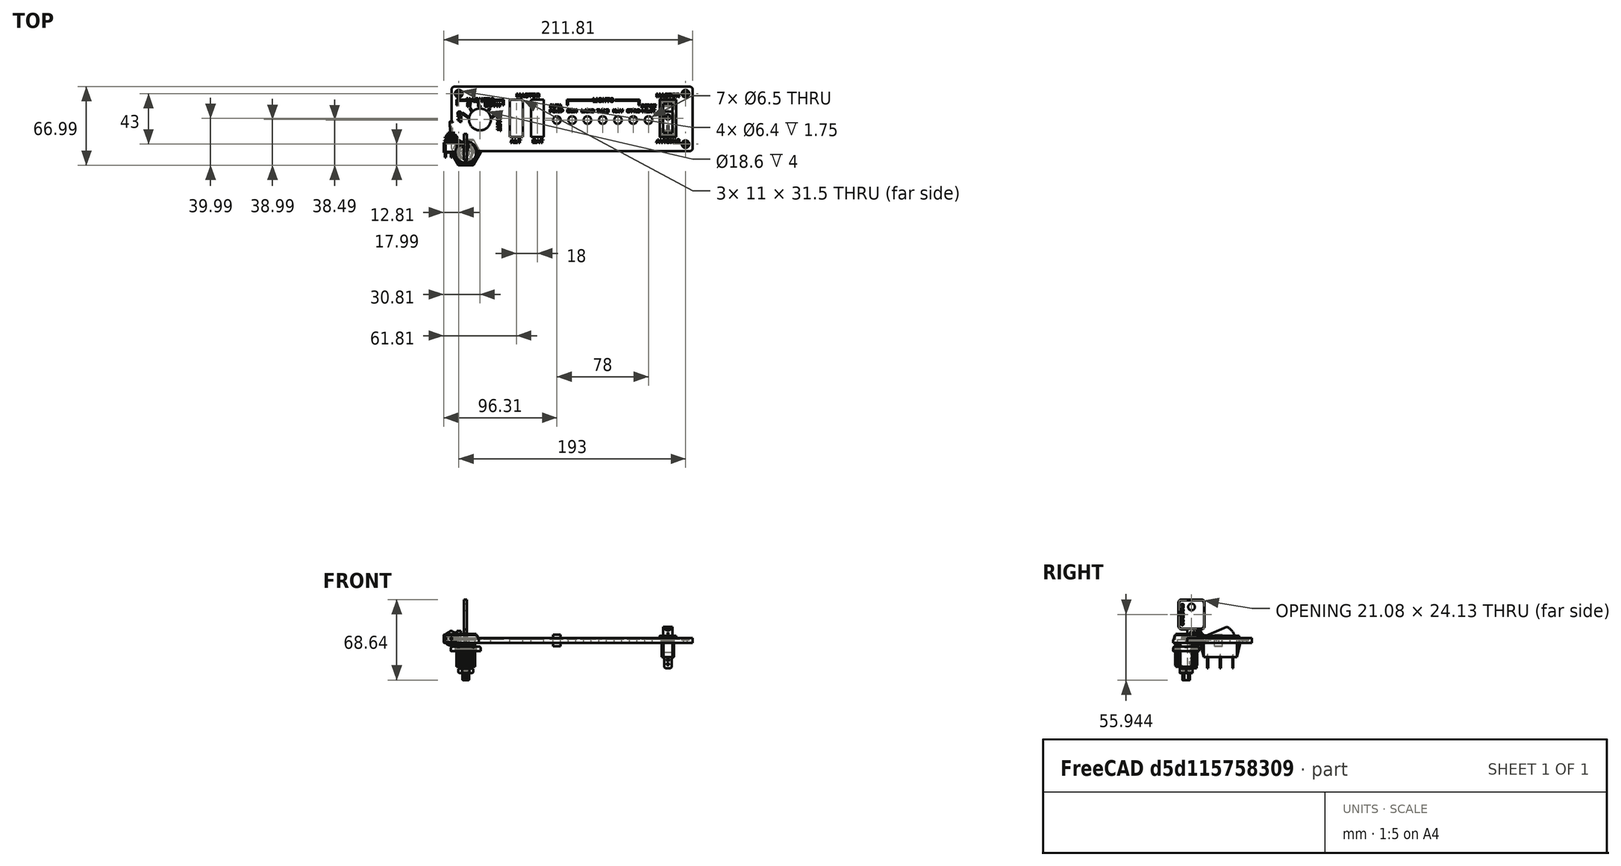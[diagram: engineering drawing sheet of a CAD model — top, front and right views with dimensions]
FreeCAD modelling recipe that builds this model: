
FCSTD DOCUMENT  (FreeCAD 0.19R24291 (Git))
Label: Frame
License: All rights reserved
LicenseURL: http://en.wikipedia.org/wiki/All_rights_reserved
objects: Part::Part2DObjectPython×22, Part::Extrusion×22, Part::Feature×17, Part::Box×15, Part::FeaturePython×8, Part::MultiFuse×5, Part::Cylinder×4, Part::Cut×3, App::Part×2, Mesh::Feature×2, App::DocumentObjectGroup×2, Part::Fillet×1
note: 93 computed .brp shape members not serialized (recipe doc carries the construction recipe); baked Part::Feature solids carry a one-line shape summary decoded from their .brp

FEATURE [Part::Feature] Part__Feature  label="SPDT Toggle Switch Base"
  Placement = pos=(-12.3077,3.81119,0) rot=(0,0,1;0rad)
  shape: bbox 13 x 8 x 7 mm, 18 faces (baked)
FEATURE [Part::Feature] Part__Feature001  label="SPDT Toggle Switch Pin"
  Placement = pos=(-5.80769,-0.188811,0) rot=(1,0,0;1.5708rad)
  shape: bbox 0.95 x 4 x 2.2 mm, 10 faces (baked)
FEATURE [Part::Feature] Part__Feature002  label="SPDT Toggle Switch Pin001"
  Placement = pos=(-0.782692,-0.188811,0) rot=(1,0,0;1.5708rad)
  shape: bbox 0.95 x 4 x 2.2 mm, 10 faces (baked)
FEATURE [Part::Feature] Part__Feature003  label="SPDT Toggle Switch Pin002"
  Placement = pos=(4.24231,-0.188811,0) rot=(1,0,0;1.5708rad)
  shape: bbox 0.95 x 4 x 2.2 mm, 10 faces (baked)
FEATURE [Part::Feature] Part__Feature004  label="SPDT Toggle Switch Treaded Tube"
  Placement = pos=(-18.8077,7.81119,0) rot=(0,0.707107,0.707107;3.14159rad)
  shape: bbox 13 x 16.4 x 7.2 mm, 28 faces, 2 solids (baked)
FEATURE [Part::Feature] Part__Feature005  label="Toggle Switch"
  Placement = pos=(-12.3077,12.4185,3.49975) rot=(1,0,0;0.000203rad)
  shape: bbox 3.001 x 13.06 x 2.999 mm, 5 faces, 2 solids (baked)
FEATURE [Part::Feature] Part__Feature006  label="M6x0.5 Hex Nut"
  Placement = pos=(-12.3077,9.81119,3.5) rot=(1,0,0;1.5708rad)
  shape: bbox 9 x 1.5 x 8.993 mm, 21 faces (baked)
FEATURE [Part::Feature] Part__Feature007  label="M6x0.5 Hex Nut001"
  Placement = pos=(-12.3077,13.0612,3.5) rot=(-1,0,0;1.5708rad)
  shape: bbox 9 x 1.5 x 8.993 mm, 21 faces (baked)
FEATURE [Part::Feature] Part__Feature008  label="SPDT Toggle Switch Anti-Rotation Washer"
  Placement = pos=(-12.3077,9.81119,3.53489) rot=(0,0.707107,0.707107;3.14159rad)
  shape: bbox 12 x 2.4 x 12.6 mm, 11 faces (baked)
FEATURE [Part::Feature] Part__Feature009  label="AS 1969 (Internal Tooth Lock Washer Type A) M6"
  Placement = pos=(-12.3077,13.0612,3.5) rot=(0,0,-1;1.5708rad)
  shape: bbox 11 x 0.75 x 11 mm, 51 faces (baked)
FEATURE [App::Part] SPDT_Toggle_Switch  label="SPDT Toggle Switch"
  Group = -> [Part__Feature,Part__Feature001,Part__Feature002,Part__Feature003,Part__Feature004,Part__Feature005,Part__Feature006,Part__Feature007,Part__Feature008,Part__Feature009]
  Origin = -> Origin
  Placement = pos=(81,15,-8) rot=(-0.57735,0.57735,0.57735;4.18879rad)
FEATURE [Part::Feature] Part__Feature010  label="Single Pole Rocker Switch"
  Placement = pos=(43,29,4) rot=(0,0,1;0rad)
  shape: bbox 14 x 34.2 x 35.15 mm, 153 faces (baked)
FEATURE [Part::Box] Box  label="Panel"
  AttacherType = Attacher::AttachEngine3D
  Height = 4
  Length = 205
  Placement = pos=(-12,1,0) rot=(0,0,1;0rad)
  Width = 55
FEATURE [Part::FeaturePython] Clone  label="Single Pole Rocker Switch001"  # Draft clone (typed FeaturePython)
  AttacherType = Attacher::AttachEngine3D
  Fuse = false
  Objects = -> [Part__Feature010]
  Placement = pos=(61,29,4) rot=(0,0,1;0rad)
  Scale = (1,1,1)
FEATURE [Part::FeaturePython] Clone001  label="Single Pole Rocker Switch002"  # Draft clone (typed FeaturePython)
  AttacherType = Attacher::AttachEngine3D
  Fuse = false
  Objects = -> [Clone]
  Placement = pos=(172,29,4) rot=(0,0,1;0rad)
  Scale = (1,1,1)
FEATURE [Part::FeaturePython] Array  label="Toggle-switch"  # Draft array (typed FeaturePython)
  Angle = 360
  ArrayType = 0
  Axis = (0,0,1)
  Base = -> SPDT_Toggle_Switch
  Center = (0,0,0)
  Count = 7
  ExpandArray = false
  Fuse = false
  IntervalAxis = (0,0,0)
  IntervalX = (13,0,0)
  IntervalY = (0,100,0)
  IntervalZ = (0,0,100)
  NumberCircles = 3
  NumberPolar = 5
  NumberX = 7
  NumberY = 1
  NumberZ = 1
  PlacementList = 7 placements: arithmetic series from (81,15,-8) step (13,0,0) to (159,15,-8)
  RadialDistance = 50
  ScaleList = (7) [(1,1,1),(1,1,1),(1,1,1),(1,1,1),(1,1,1),(1,1,1),(1,1,1)]
  Symmetry = 1
  TangentialDistance = 25
FEATURE [Mesh::Feature] key_switch
  Placement = pos=(29,14,-28) rot=(0,1,0;4.71239rad)
FEATURE [Mesh::Feature] Redesigned_Spring_Back_Handle
  Placement = pos=(12.0268,26.0291,24) rot=(0.891007,-0.45399,0;3.14159rad)
FEATURE [Part::Feature] Part__Feature011  label="Outer-Medeco-Lock"
  shape: bbox 23.78 x 23.78 x 28.32 mm, 471 faces (baked)
FEATURE [Part::Feature] Part__Feature012  label="Inner-Medeco-Lock"
  Placement = pos=(-2e-15,1e-15,7.62) rot=(0,0,1;0rad)
  shape: bbox 17.78 x 17.65 x 39.37 mm, 346 faces (baked)
FEATURE [Part::Feature] Part__Feature013  label="Washer-4-Lock-Latch"
  Placement = pos=(0,0,-21.463) rot=(0,0,1;0.134093rad)
  shape: bbox 12.7 x 12.7 x 0.889 mm, 6 faces (baked)
FEATURE [Part::Feature] Part__Feature014  label="Nut-4-Lock-Latch"
  Placement = pos=(0,0,-23.8125) rot=(0,0,1;0rad)
  shape: bbox 12.61 x 12.61 x 4.193 mm, 14 faces (baked)
FEATURE [Part::Feature] Part__Feature015  label="Nut-4-Medeco-Lock"
  Placement = pos=(-1e-15,0,-5.1562) rot=(0,0,1;0rad)
  shape: bbox 25.37 x 21.97 x 3.962 mm, 29 faces (baked)
FEATURE [Part::Feature] Part__Feature016  label="Key-4-Medeco-Lock"
  Placement = pos=(-1.52743,4.52303,24.1935) rot=(0,0,1;0rad)
  shape: bbox 2.54 x 22.23 x 57.15 mm, 273 faces (baked)
FEATURE [App::Part] STEP_LOCK_and_KEY  label="STEP LOCK_and_KEY"
  Group = -> [Part__Feature011,Part__Feature012,Part__Feature013,Part__Feature014,Part__Feature015,Part__Feature016]
  Origin = -> Origin001
  Placement = pos=(12,27,4) rot=(0,0,1;0rad)
FEATURE [Part::Box] Box001  label="hueco_rocket"
  AttacherType = Attacher::AttachEngine3D
  Height = 10
  Length = 11
  Placement = pos=(37.5,13.25,-3) rot=(0,0,1;0rad)
  Width = 31.5
FEATURE [Part::FeaturePython] Clone002  label="hueco_rocket001"  # Draft clone (typed FeaturePython)
  AttacherType = Attacher::AttachEngine3D
  Fuse = false
  Objects = -> [Box001]
  Placement = pos=(55.5,13.25,-3) rot=(0,0,1;0rad)
  Scale = (1,1,1)
FEATURE [Part::FeaturePython] Clone003  label="hueco_rocket002"  # Draft clone (typed FeaturePython)
  AttacherType = Attacher::AttachEngine3D
  Fuse = false
  Objects = -> [Clone002]
  Placement = pos=(166.5,13.25,-3) rot=(0,0,1;0rad)
  Scale = (1,1,1)
FEATURE [Part::Cylinder] Cylinder  label="Cilindro"
  Angle = 360
  AttacherType = Attacher::AttachEngine3D
  Height = 10
  Placement = pos=(77.5,27.5,-3) rot=(0,0,1;0rad)
  Radius = 3.25
FEATURE [Part::FeaturePython] Array001  label="Array_agujeros_interr"  # Draft array (typed FeaturePython)
  Angle = 360
  ArrayType = 0
  Axis = (0,0,1)
  Base = -> Cylinder
  Center = (0,0,0)
  Count = 7
  ExpandArray = false
  Fuse = false
  IntervalAxis = (0,0,0)
  IntervalX = (13,0,0)
  IntervalY = (0,100,0)
  IntervalZ = (0,0,100)
  NumberCircles = 3
  NumberPolar = 5
  NumberX = 7
  NumberY = 1
  NumberZ = 1
  PlacementList = 7 placements: arithmetic series from (77.5,27.5,-3) step (13,0,0) to (155.5,27.5,-3)
  RadialDistance = 50
  ScaleList = (7) [(1,1,1),(1,1,1),(1,1,1),(1,1,1),(1,1,1),(1,1,1),(1,1,1)]
  Symmetry = 1
  TangentialDistance = 25
FEATURE [Part::Cylinder] Cylinder001  label="Agujero_llave"
  Angle = 360
  AttacherType = Attacher::AttachEngine3D
  Height = 10
  Placement = pos=(12,28,-3) rot=(0,0,1;0rad)
  Radius = 9.3
FEATURE [Part::MultiFuse] Fusion  label="Agujeros"
  Shapes = -> [Cylinder001,Array001,Clone003,Clone002,Box001]
FEATURE [Part::Cut] Cut  label="Panel_con_agujeros_interr"
  Base = -> Box
  Tool = -> Fusion
FEATURE [Part::Cylinder] Cylinder002  label="Cilindro001"
  Angle = 360
  AttacherType = Attacher::AttachEngine3D
  Height = 10
  Placement = pos=(-6,7,0) rot=(0,0,1;0rad)
  Radius = 1.7
FEATURE [Part::Cylinder] Cylinder003  label="Cilindro002"
  Angle = 360
  AttacherType = Attacher::AttachEngine3D
  Height = 1.8
  Placement = pos=(-6,7,2.25) rot=(0,0,1;0rad)
  Radius = 3.2
FEATURE [Part::FeaturePython] Array002  label="agujeros_tornillos"  # Draft array (typed FeaturePython)
  Angle = 360
  ArrayType = 0
  Axis = (0,0,1)
  Base = -> Cylinder002
  Center = (0,0,0)
  Count = 4
  ExpandArray = false
  Fuse = false
  IntervalAxis = (0,0,0)
  IntervalX = (193,0,0)
  IntervalY = (0,43,0)
  IntervalZ = (0,0,100)
  NumberCircles = 3
  NumberPolar = 5
  NumberX = 2
  NumberY = 2
  NumberZ = 1
  PlacementList = 4 placements: [(-6,7,0),(-6,50,0),(187,7,0),(187,50,0)]
  RadialDistance = 50
  ScaleList = (4) [(1,1,1),(1,1,1),(1,1,1),(1,1,1)]
  Symmetry = 1
  TangentialDistance = 25
FEATURE [Part::FeaturePython] Array003  label="avellanado"  # Draft array (typed FeaturePython)
  Angle = 360
  ArrayType = 0
  Axis = (0,0,1)
  Base = -> Cylinder003
  Center = (0,0,0)
  Count = 4
  ExpandArray = false
  Fuse = false
  IntervalAxis = (0,0,0)
  IntervalX = (193,0,0)
  IntervalY = (0,43,0)
  IntervalZ = (0,0,100)
  NumberCircles = 3
  NumberPolar = 5
  NumberX = 2
  NumberY = 2
  NumberZ = 1
  PlacementList = 4 placements: [(-6,7,2.25),(-6,50,2.25),(187,7,2.25),(187,50,2.25)]
  RadialDistance = 50
  ScaleList = (4) [(1,1,1),(1,1,1),(1,1,1),(1,1,1)]
  Symmetry = 1
  TangentialDistance = 25
FEATURE [Part::MultiFuse] Fusion001  label="Agujeros_sujecion"
  Shapes = -> [Array003,Array002]
FEATURE [Part::Cut] Cut001  label="Panel_taladrado"
  Base = -> Cut
  Tool = -> Fusion001
FEATURE [Part::Part2DObjectPython] ShapeString  # Draft 2D object (typed FeaturePython)
  FontFile = <path> Simulador/18.- Switch panel Cessna (propio) con PCB/cessna-switch-panel/Frame-design/arial-black_[allfont.es].ttf
  Placement = pos=(43,47,4) rot=(0,0,1;0rad)
  Size = 4
  String = MASTER
  Tracking = 0
FEATURE [Part::Part2DObjectPython] ShapeString001  # Draft 2D object (typed FeaturePython)
  FontFile = <path> Simulador/18.- Switch panel Cessna (propio) con PCB/cessna-switch-panel/Frame-design/arial-black_[allfont.es].ttf
  Placement = pos=(38,8,4) rot=(0,0,1;0rad)
  Size = 4
  String = ALT
  Tracking = 0
FEATURE [Part::Part2DObjectPython] ShapeString002  # Draft 2D object (typed FeaturePython)
  FontFile = <path> Simulador/18.- Switch panel Cessna (propio) con PCB/cessna-switch-panel/Frame-design/arial-black_[allfont.es].ttf
  Placement = pos=(56.5,8,4) rot=(0,0,1;0rad)
  Size = 4
  String = BAT
  Tracking = 0
FEATURE [Part::Part2DObjectPython] ShapeString003  # Draft 2D object (typed FeaturePython)
  FontFile = <path> Simulador/18.- Switch panel Cessna (propio) con PCB/cessna-switch-panel/Frame-design/arial-black_[allfont.es].ttf
  Placement = pos=(108,43,4) rot=(0,0,1;0rad)
  Size = 4
  String = LIGHTS
  Tracking = 0
FEATURE [Part::Part2DObjectPython] ShapeString004  # Draft 2D object (typed FeaturePython)
  FontFile = <path> Simulador/18.- Switch panel Cessna (propio) con PCB/cessna-switch-panel/Frame-design/arial-black_[allfont.es].ttf
  Placement = pos=(71,34,4) rot=(0,0,1;0rad)
  Size = 3.5
  String = PUMP
  Tracking = 0
FEATURE [Part::Part2DObjectPython] ShapeString005  # Draft 2D object (typed FeaturePython)
  FontFile = <path> Simulador/18.- Switch panel Cessna (propio) con PCB/cessna-switch-panel/Frame-design/arial-black_[allfont.es].ttf
  Placement = pos=(71.4,38,4) rot=(0,0,1;0rad)
  Size = 3.5
  String = FUEL
  Tracking = 0
FEATURE [Part::Part2DObjectPython] ShapeString006  # Draft 2D object (typed FeaturePython)
  FontFile = <path> Simulador/18.- Switch panel Cessna (propio) con PCB/cessna-switch-panel/Frame-design/arial-black_[allfont.es].ttf
  Placement = pos=(86,34,4) rot=(0,0,1;0rad)
  Size = 3.5
  String = BCN
  Tracking = 0
FEATURE [Part::Part2DObjectPython] ShapeString007  # Draft 2D object (typed FeaturePython)
  FontFile = <path> Simulador/18.- Switch panel Cessna (propio) con PCB/cessna-switch-panel/Frame-design/arial-black_[allfont.es].ttf
  Placement = pos=(98,34,4) rot=(0,0,1;0rad)
  Size = 3.5
  String = LAND
  Tracking = 0
FEATURE [Part::Part2DObjectPython] ShapeString008  # Draft 2D object (typed FeaturePython)
  FontFile = <path> Simulador/18.- Switch panel Cessna (propio) con PCB/cessna-switch-panel/Frame-design/arial-black_[allfont.es].ttf
  Placement = pos=(111.5,34,4.1) rot=(0,0,1;0rad)
  Size = 3.5
  String = TA
  Tracking = 0
FEATURE [Part::Part2DObjectPython] ShapeString009  # Draft 2D object (typed FeaturePython)
  FontFile = <path> Simulador/18.- Switch panel Cessna (propio) con PCB/cessna-switch-panel/Frame-design/arial-black_[allfont.es].ttf
  Placement = pos=(125,34,4) rot=(0,0,1;0rad)
  Size = 3.5
  String = NAV
  Tracking = 0
FEATURE [Part::Part2DObjectPython] ShapeString010  # Draft 2D object (typed FeaturePython)
  FontFile = <path> Simulador/18.- Switch panel Cessna (propio) con PCB/cessna-switch-panel/Frame-design/arial-black_[allfont.es].ttf
  Placement = pos=(137,34,4) rot=(0,0,1;0rad)
  Size = 3.5
  String = STRO
  Tracking = 0
FEATURE [Part::Part2DObjectPython] ShapeString011  # Draft 2D object (typed FeaturePython)
  FontFile = <path> Simulador/18.- Switch panel Cessna (propio) con PCB/cessna-switch-panel/Frame-design/arial-black_[allfont.es].ttf
  Placement = pos=(150,34,4) rot=(0,0,1;0rad)
  Size = 3.5
  String = HEAT
  Tracking = 0
FEATURE [Part::Part2DObjectPython] ShapeString012  # Draft 2D object (typed FeaturePython)
  FontFile = <path> Simulador/18.- Switch panel Cessna (propio) con PCB/cessna-switch-panel/Frame-design/arial-black_[allfont.es].ttf
  Placement = pos=(149.4,38,4) rot=(0,0,1;0rad)
  Size = 3.5
  String = PITOT
  Tracking = 0
FEATURE [Part::Part2DObjectPython] ShapeString013  # Draft 2D object (typed FeaturePython)
  FontFile = <path> Simulador/18.- Switch panel Cessna (propio) con PCB/cessna-switch-panel/Frame-design/arial-black_[allfont.es].ttf
  Placement = pos=(162,47,4) rot=(0,0,1;0rad)
  Size = 4
  String = MASTER
  Tracking = 0
FEATURE [Part::Part2DObjectPython] ShapeString014  # Draft 2D object (typed FeaturePython)
  FontFile = <path> Simulador/18.- Switch panel Cessna (propio) con PCB/cessna-switch-panel/Frame-design/arial-black_[allfont.es].ttf
  Placement = pos=(162,8,4) rot=(0,0,1;0rad)
  Size = 4
  String = AVIONIC
  Tracking = 0
FEATURE [Part::Box] Box002  label="Cubo"
  AttacherType = Attacher::AttachEngine3D
  Height = 0.8
  Length = 1
  Placement = pos=(86,40,3.2) rot=(0,0,1;0rad)
  Width = 4
FEATURE [Part::Box] Box003  label="Cubo004"
  AttacherType = Attacher::AttachEngine3D
  Height = 0.8
  Length = 21
  Placement = pos=(86,44,3.2) rot=(0,0,1;0rad)
  Width = 1
FEATURE [Part::Box] Box004  label="Cubo005"
  AttacherType = Attacher::AttachEngine3D
  Height = 0.8
  Length = 21
  Placement = pos=(127,44,3.2) rot=(0,0,1;0rad)
  Width = 1
FEATURE [Part::Box] Box005  label="Cubo006"
  AttacherType = Attacher::AttachEngine3D
  Height = 0.8
  Length = 1
  Placement = pos=(147,40,3.2) rot=(0,0,1;0rad)
  Width = 4
FEATURE [Part::Part2DObjectPython] ShapeString015  # Draft 2D object (typed FeaturePython)
  FontFile = <path> Simulador/18.- Switch panel Cessna (propio) con PCB/cessna-switch-panel/Frame-design/arial-black_[allfont.es].ttf
  Placement = pos=(0.2,43,4) rot=(0,0,1;0rad)
  Size = 4
  String = MAGNETO
  Tracking = 0
FEATURE [Part::Box] Box006  label="Cubo007"
  AttacherType = Attacher::AttachEngine3D
  Height = 0.8
  Length = 1
  Placement = pos=(-8,40,3.2) rot=(0,0,1;0rad)
  Width = 4
FEATURE [Part::Box] Box007  label="Cubo008"
  AttacherType = Attacher::AttachEngine3D
  Height = 0.8
  Length = 7.5
  Placement = pos=(-8,44,3.2) rot=(0,0,1;0rad)
  Width = 1
FEATURE [Part::Box] Box008  label="Cubo009"
  AttacherType = Attacher::AttachEngine3D
  Height = 0.8
  Length = 1
  Placement = pos=(31.5,40,3.2) rot=(0,0,1;0rad)
  Width = 4
FEATURE [Part::Box] Box009  label="Cubo010"
  AttacherType = Attacher::AttachEngine3D
  Height = 0.8
  Length = 7.5
  Placement = pos=(25,44,3.2) rot=(0,0,1;0rad)
  Width = 1
FEATURE [Part::Box] Box010  label="Cubo011"
  AttacherType = Attacher::AttachEngine3D
  Height = 0.8
  Length = 1
  Placement = pos=(4,28,3.2) rot=(0,0,1;0.959931rad)
  Width = 9
FEATURE [Part::Box] Box011  label="Cubo012"
  AttacherType = Attacher::AttachEngine3D
  Height = 0.8
  Length = 1
  Placement = pos=(5,34,3.2) rot=(0,0,1;0.506145rad)
  Width = 4
FEATURE [Part::Box] Box012  label="Cubo013"
  AttacherType = Attacher::AttachEngine3D
  Height = 0.8
  Length = 1
  Placement = pos=(11,33.5,3.2) rot=(0,0,1;0rad)
  Width = 5
FEATURE [Part::Box] Box013  label="Cubo014"
  AttacherType = Attacher::AttachEngine3D
  Height = 0.8
  Length = 1
  Placement = pos=(18,34.5,3.2) rot=(0,0,-1;0.506145rad)
  Width = 4
FEATURE [Part::Box] Box014  label="Cubo015"
  AttacherType = Attacher::AttachEngine3D
  Height = 0.8
  Length = 1
  Placement = pos=(19,28,3.2) rot=(0,0,-1;0.959931rad)
  Width = 8
FEATURE [Part::Part2DObjectPython] ShapeString016  # Draft 2D object (typed FeaturePython)
  FontFile = <path> Simulador/18.- Switch panel Cessna (propio) con PCB/cessna-switch-panel/Frame-design/arial-black_[allfont.es].ttf
  Placement = pos=(1,39,4) rot=(0,0,1;0rad)
  Size = 4
  String = R
  Tracking = 0
FEATURE [Part::Part2DObjectPython] ShapeString017  # Draft 2D object (typed FeaturePython)
  FontFile = <path> Simulador/18.- Switch panel Cessna (propio) con PCB/cessna-switch-panel/Frame-design/arial-black_[allfont.es].ttf
  Placement = pos=(10,39,4) rot=(0,0,1;0rad)
  Size = 4
  String = L
  Tracking = 0
FEATURE [Part::Part2DObjectPython] ShapeString018  # Draft 2D object (typed FeaturePython)
  FontFile = <path> Simulador/18.- Switch panel Cessna (propio) con PCB/cessna-switch-panel/Frame-design/arial-black_[allfont.es].ttf
  Placement = pos=(16,39,4) rot=(0,0,1;0rad)
  Size = 4
  String = BOTH
  Tracking = 0
FEATURE [Part::Part2DObjectPython] ShapeString019  # Draft 2D object (typed FeaturePython)
  FontFile = <path> Simulador/18.- Switch panel Cessna (propio) con PCB/cessna-switch-panel/Frame-design/arial-black_[allfont.es].ttf
  Placement = pos=(26.8,34,4) rot=(0,0,-1;1.5708rad)
  Size = 4
  String = START
  Tracking = 0
FEATURE [Part::Part2DObjectPython] ShapeString020  # Draft 2D object (typed FeaturePython)
  FontFile = <path> Simulador/18.- Switch panel Cessna (propio) con PCB/cessna-switch-panel/Frame-design/arial-black_[allfont.es].ttf
  Placement = pos=(-7,35,4) rot=(0,0,-1;1.5708rad)
  Size = 4
  String = OFF
  Tracking = 0
FEATURE [Part::MultiFuse] Fusion003  label="hueco_magneto"
  Shapes = -> [Box014,Box013,Box012,Box011,Box010,Box009,Box008,Box007,Box006]
FEATURE [Part::MultiFuse] Fusion004  label="hueco_light"
  Shapes = -> [Box005,Box004,Box003,Box002]
FEATURE [Part::Extrusion] Extrude
  Base = -> ShapeString
  Dir = (0,0,1)
  DirMode = 2
  FaceMakerClass = Part::FaceMakerBullseye
  LengthFwd = -0.8
  LengthRev = 0
  Solid = false
  Symmetric = false
FEATURE [Part::Extrusion] Extrude001
  Base = -> ShapeString001
  Dir = (0,0,1)
  DirMode = 2
  FaceMakerClass = Part::FaceMakerBullseye
  LengthFwd = -0.8
  LengthRev = 0
  Solid = false
  Symmetric = false
FEATURE [Part::Extrusion] Extrude002
  Base = -> ShapeString002
  Dir = (0,0,1)
  DirMode = 2
  FaceMakerClass = Part::FaceMakerBullseye
  LengthFwd = -0.8
  LengthRev = 0
  Solid = false
  Symmetric = false
FEATURE [Part::Extrusion] Extrude003
  Base = -> ShapeString003
  Dir = (0,0,1)
  DirMode = 2
  FaceMakerClass = Part::FaceMakerBullseye
  LengthFwd = -0.8
  LengthRev = 0
  Solid = false
  Symmetric = false
FEATURE [Part::Extrusion] Extrude004
  Base = -> ShapeString004
  Dir = (0,0,1)
  DirMode = 2
  FaceMakerClass = Part::FaceMakerBullseye
  LengthFwd = -0.8
  LengthRev = 0
  Solid = false
  Symmetric = false
FEATURE [Part::Extrusion] Extrude005
  Base = -> ShapeString005
  Dir = (0,0,1)
  DirMode = 2
  FaceMakerClass = Part::FaceMakerBullseye
  LengthFwd = -0.8
  LengthRev = 0
  Solid = false
  Symmetric = false
FEATURE [Part::Extrusion] Extrude006
  Base = -> ShapeString006
  Dir = (0,0,1)
  DirMode = 2
  FaceMakerClass = Part::FaceMakerBullseye
  LengthFwd = -0.8
  LengthRev = 0
  Solid = false
  Symmetric = false
FEATURE [Part::Extrusion] Extrude007
  Base = -> ShapeString007
  Dir = (0,0,1)
  DirMode = 2
  FaceMakerClass = Part::FaceMakerBullseye
  LengthFwd = -0.8
  LengthRev = 0
  Solid = false
  Symmetric = false
FEATURE [Part::Extrusion] Extrude008
  Base = -> ShapeString008
  Dir = (0,0,1)
  DirMode = 2
  FaceMakerClass = Part::FaceMakerBullseye
  LengthFwd = -0.8
  LengthRev = 0
  Solid = false
  Symmetric = false
FEATURE [Part::Extrusion] Extrude009
  Base = -> ShapeString009
  Dir = (0,0,1)
  DirMode = 2
  FaceMakerClass = Part::FaceMakerBullseye
  LengthFwd = -0.8
  LengthRev = 0
  Solid = false
  Symmetric = false
FEATURE [Part::Extrusion] Extrude010
  Base = -> ShapeString010
  Dir = (0,0,1)
  DirMode = 2
  FaceMakerClass = Part::FaceMakerBullseye
  LengthFwd = -0.8
  LengthRev = 0
  Solid = false
  Symmetric = false
FEATURE [Part::Extrusion] Extrude011
  Base = -> ShapeString011
  Dir = (0,0,1)
  DirMode = 2
  FaceMakerClass = Part::FaceMakerBullseye
  LengthFwd = -0.8
  LengthRev = 0
  Solid = false
  Symmetric = false
FEATURE [Part::Extrusion] Extrude012
  Base = -> ShapeString012
  Dir = (0,0,1)
  DirMode = 2
  FaceMakerClass = Part::FaceMakerBullseye
  LengthFwd = -0.8
  LengthRev = 0
  Solid = false
  Symmetric = false
FEATURE [Part::Extrusion] Extrude013
  Base = -> ShapeString013
  Dir = (0,0,1)
  DirMode = 2
  FaceMakerClass = Part::FaceMakerBullseye
  LengthFwd = -0.8
  LengthRev = 0
  Solid = false
  Symmetric = false
FEATURE [Part::Extrusion] Extrude014
  Base = -> ShapeString014
  Dir = (0,0,1)
  DirMode = 2
  FaceMakerClass = Part::FaceMakerBullseye
  LengthFwd = -0.8
  LengthRev = 0
  Solid = false
  Symmetric = false
FEATURE [Part::Extrusion] Extrude015
  Base = -> ShapeString015
  Dir = (0,0,1)
  DirMode = 2
  FaceMakerClass = Part::FaceMakerBullseye
  LengthFwd = -0.8
  LengthRev = 0
  Solid = false
  Symmetric = false
FEATURE [Part::Extrusion] Extrude016
  Base = -> ShapeString016
  Dir = (0,0,1)
  DirMode = 2
  FaceMakerClass = Part::FaceMakerBullseye
  LengthFwd = -0.8
  LengthRev = 0
  Solid = false
  Symmetric = false
FEATURE [Part::Extrusion] Extrude017
  Base = -> ShapeString017
  Dir = (0,0,1)
  DirMode = 2
  FaceMakerClass = Part::FaceMakerBullseye
  LengthFwd = -0.8
  LengthRev = 0
  Solid = false
  Symmetric = false
FEATURE [Part::Extrusion] Extrude018
  Base = -> ShapeString018
  Dir = (0,0,1)
  DirMode = 2
  FaceMakerClass = Part::FaceMakerBullseye
  LengthFwd = -0.8
  LengthRev = 0
  Solid = false
  Symmetric = false
FEATURE [Part::Extrusion] Extrude019
  Base = -> ShapeString019
  Dir = (0,0,1)
  DirMode = 2
  FaceMakerClass = Part::FaceMakerBullseye
  LengthFwd = -0.8
  LengthRev = 0
  Solid = false
  Symmetric = false
FEATURE [Part::Extrusion] Extrude020
  Base = -> ShapeString020
  Dir = (0,0,1)
  DirMode = 2
  FaceMakerClass = Part::FaceMakerBullseye
  LengthFwd = -0.8
  LengthRev = 0
  Solid = false
  Symmetric = false
FEATURE [Part::Part2DObjectPython] ShapeString021  # Draft 2D object (typed FeaturePython)
  FontFile = <path> Simulador/18.- Switch panel Cessna (propio) con PCB/cessna-switch-panel/Frame-design/arial-black_[allfont.es].ttf
  Placement = pos=(117.5,34,4.1) rot=(0,0,1;0rad)
  Size = 3.5
  String = XI
  Tracking = 0
FEATURE [Part::Extrusion] Extrude021
  Base = -> ShapeString021
  Dir = (0,0,1)
  DirMode = 2
  FaceMakerClass = Part::FaceMakerBullseye
  LengthFwd = -0.8
  LengthRev = 0
  Solid = false
  Symmetric = false
FEATURE [Part::MultiFuse] Fusion005  label="Grabados"
  Shapes = -> [Fusion003,Fusion004,Extrude,Extrude001,Extrude002,Extrude003,Extrude004,Extrude005,Extrude006,Extrude007,Extrude008,Extrude009,Extrude010,Extrude011,Extrude012,Extrude013,Extrude014,Extrude015,Extrude016,Extrude017,Extrude018,Extrude019,Extrude020,Extrude021]
FEATURE [Part::Cut] Cut002  label="Panel_grabado_switches"
  Base = -> Cut001
  Tool = -> Fusion005
FEATURE [Part::Fillet] Fillet  label="Panel_grabado_switches_bordes_red"
  Base = -> Cut002
  Edges = 4 edges r=2.5: [Edge1,Edge3,Edge6,Edge1094]
FEATURE [App::DocumentObjectGroup] Group  label="Botones"
  Group = -> [STEP_LOCK_and_KEY,Clone001,Clone,Part__Feature010,Array]
FEATURE [App::DocumentObjectGroup] Group001  label="Estructura llave"
  Group = -> [key_switch,Redesigned_Spring_Back_Handle]
note: 22 file-system paths scrubbed to <path> (originals preserved in the JSON sidecar)
